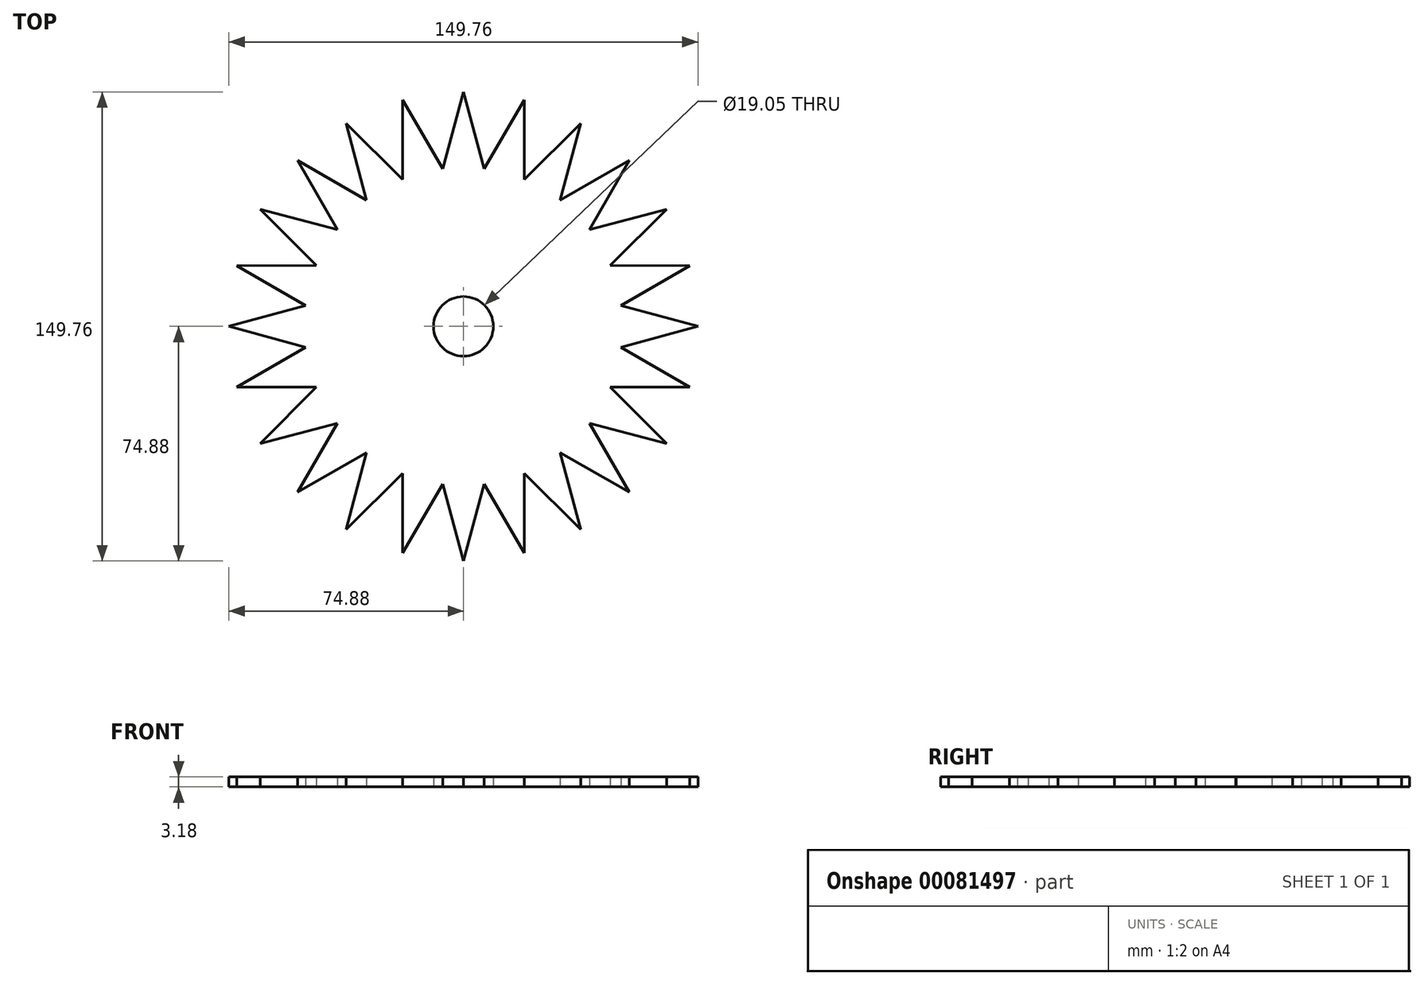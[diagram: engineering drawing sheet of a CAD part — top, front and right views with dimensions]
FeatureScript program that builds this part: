
annotation { "Feature Type Name" : "Feature", "Feature Type Description" : "" }
export const myFeature = defineFeature(function(context is Context, id is Id, definition is map)
    precondition{}
    {
        {
            var Q0;
            Q0=qCreatedBy(makeId("Top.planeOp"),FACE);
            var sketch = newSketch(context, id + "F0", { "sketchPlane" : qUnion([Q0])});
            skLineSegment(sketch, "E0", {"start": v(-6.63, 50.37) * mm, "end": v(0, 74.88) * mm});
            skLineSegment(sketch, "E1", {"start": v(0, 74.88) * mm, "end": v(6.63, 50.37) * mm});
            skLineSegment(sketch, "E2.1.0", {"start": v(-19.38, 72.33) * mm, "end": v(-6.63, 50.37) * mm});
            skLineSegment(sketch, "E2.1.1", {"start": v(-19.44, 46.93) * mm, "end": v(-19.38, 72.33) * mm});
            skLineSegment(sketch, "E2.2.0", {"start": v(-37.44, 64.85) * mm, "end": v(-19.44, 46.93) * mm});
            skLineSegment(sketch, "E2.2.1", {"start": v(-30.93, 40.3) * mm, "end": v(-37.44, 64.85) * mm});
            skLineSegment(sketch, "E2.3.0", {"start": v(-52.95, 52.95) * mm, "end": v(-30.93, 40.3) * mm});
            skLineSegment(sketch, "E2.3.1", {"start": v(-40.3, 30.93) * mm, "end": v(-52.95, 52.95) * mm});
            skLineSegment(sketch, "E2.4.0", {"start": v(-64.85, 37.44) * mm, "end": v(-40.3, 30.93) * mm});
            skLineSegment(sketch, "E2.4.1", {"start": v(-46.93, 19.44) * mm, "end": v(-64.85, 37.44) * mm});
            skLineSegment(sketch, "E2.5.0", {"start": v(-72.33, 19.38) * mm, "end": v(-46.93, 19.44) * mm});
            skLineSegment(sketch, "E2.5.1", {"start": v(-50.37, 6.63) * mm, "end": v(-72.33, 19.38) * mm});
            skLineSegment(sketch, "E2.6.0", {"start": v(-74.88, 0) * mm, "end": v(-50.37, 6.63) * mm});
            skLineSegment(sketch, "E2.6.1", {"start": v(-50.37, -6.63) * mm, "end": v(-74.88, 0) * mm});
            skLineSegment(sketch, "E2.7.0", {"start": v(-72.33, -19.38) * mm, "end": v(-50.37, -6.63) * mm});
            skLineSegment(sketch, "E2.7.1", {"start": v(-46.93, -19.44) * mm, "end": v(-72.33, -19.38) * mm});
            skLineSegment(sketch, "E2.8.0", {"start": v(-64.85, -37.44) * mm, "end": v(-46.93, -19.44) * mm});
            skLineSegment(sketch, "E2.8.1", {"start": v(-40.3, -30.93) * mm, "end": v(-64.85, -37.44) * mm});
            skLineSegment(sketch, "E2.9.0", {"start": v(-52.95, -52.95) * mm, "end": v(-40.3, -30.93) * mm});
            skLineSegment(sketch, "E2.9.1", {"start": v(-30.93, -40.3) * mm, "end": v(-52.95, -52.95) * mm});
            skLineSegment(sketch, "E2.10.0", {"start": v(-37.44, -64.85) * mm, "end": v(-30.93, -40.3) * mm});
            skLineSegment(sketch, "E2.10.1", {"start": v(-19.44, -46.93) * mm, "end": v(-37.44, -64.85) * mm});
            skLineSegment(sketch, "E2.11.0", {"start": v(-19.38, -72.33) * mm, "end": v(-19.44, -46.93) * mm});
            skLineSegment(sketch, "E2.11.1", {"start": v(-6.63, -50.37) * mm, "end": v(-19.38, -72.33) * mm});
            skLineSegment(sketch, "E2.12.0", {"start": v(0, -74.88) * mm, "end": v(-6.63, -50.37) * mm});
            skLineSegment(sketch, "E2.12.1", {"start": v(6.63, -50.37) * mm, "end": v(0, -74.88) * mm});
            skLineSegment(sketch, "E2.13.0", {"start": v(19.38, -72.33) * mm, "end": v(6.63, -50.37) * mm});
            skLineSegment(sketch, "E2.13.1", {"start": v(19.44, -46.93) * mm, "end": v(19.38, -72.33) * mm});
            skLineSegment(sketch, "E2.14.0", {"start": v(37.44, -64.85) * mm, "end": v(19.44, -46.93) * mm});
            skLineSegment(sketch, "E2.14.1", {"start": v(30.93, -40.3) * mm, "end": v(37.44, -64.85) * mm});
            skLineSegment(sketch, "E2.15.0", {"start": v(52.95, -52.95) * mm, "end": v(30.93, -40.3) * mm});
            skLineSegment(sketch, "E2.15.1", {"start": v(40.3, -30.93) * mm, "end": v(52.95, -52.95) * mm});
            skLineSegment(sketch, "E2.16.0", {"start": v(64.85, -37.44) * mm, "end": v(40.3, -30.93) * mm});
            skLineSegment(sketch, "E2.16.1", {"start": v(46.93, -19.44) * mm, "end": v(64.85, -37.44) * mm});
            skLineSegment(sketch, "E2.17.0", {"start": v(72.33, -19.38) * mm, "end": v(46.93, -19.44) * mm});
            skLineSegment(sketch, "E2.17.1", {"start": v(50.37, -6.63) * mm, "end": v(72.33, -19.38) * mm});
            skLineSegment(sketch, "E2.18.0", {"start": v(74.88, 0) * mm, "end": v(50.37, -6.63) * mm});
            skLineSegment(sketch, "E2.18.1", {"start": v(50.37, 6.63) * mm, "end": v(74.88, 0) * mm});
            skLineSegment(sketch, "E2.19.0", {"start": v(72.33, 19.38) * mm, "end": v(50.37, 6.63) * mm});
            skLineSegment(sketch, "E2.19.1", {"start": v(46.93, 19.44) * mm, "end": v(72.33, 19.38) * mm});
            skLineSegment(sketch, "E2.20.0", {"start": v(64.85, 37.44) * mm, "end": v(46.93, 19.44) * mm});
            skLineSegment(sketch, "E2.20.1", {"start": v(40.3, 30.93) * mm, "end": v(64.85, 37.44) * mm});
            skLineSegment(sketch, "E2.21.0", {"start": v(52.95, 52.95) * mm, "end": v(40.3, 30.93) * mm});
            skLineSegment(sketch, "E2.21.1", {"start": v(30.93, 40.3) * mm, "end": v(52.95, 52.95) * mm});
            skLineSegment(sketch, "E2.22.0", {"start": v(37.44, 64.85) * mm, "end": v(30.93, 40.3) * mm});
            skLineSegment(sketch, "E2.22.1", {"start": v(19.44, 46.93) * mm, "end": v(37.44, 64.85) * mm});
            skLineSegment(sketch, "E2.23.0", {"start": v(19.38, 72.33) * mm, "end": v(19.44, 46.93) * mm});
            skLineSegment(sketch, "E2.23.1", {"start": v(6.63, 50.37) * mm, "end": v(19.38, 72.33) * mm});
            skPoint(sketch, "E2.center", {"position": v(0, 0) * mm});
            skCircle(sketch, "E3", {"center": v(0, 0) * mm, "radius": 9.53 * mm});
            skSolve(sketch);
        }
        {
            var Q0;
            Q0=makeQuery(id+"F0.imprint","IMPRINT",FACE,{"disambiguationData":[TD([[makeQuery(id+"F0.imprint","IMPRINT",EDGE,{"derivedFrom":sQuery(id+"F0.wireOp",EDGE,"E0")}),-1.0]])]});
            extrude(context, id + "F1", {"entities" : qUnion([Q0]), "depth" : 3.17 * mm});
        }
    });
